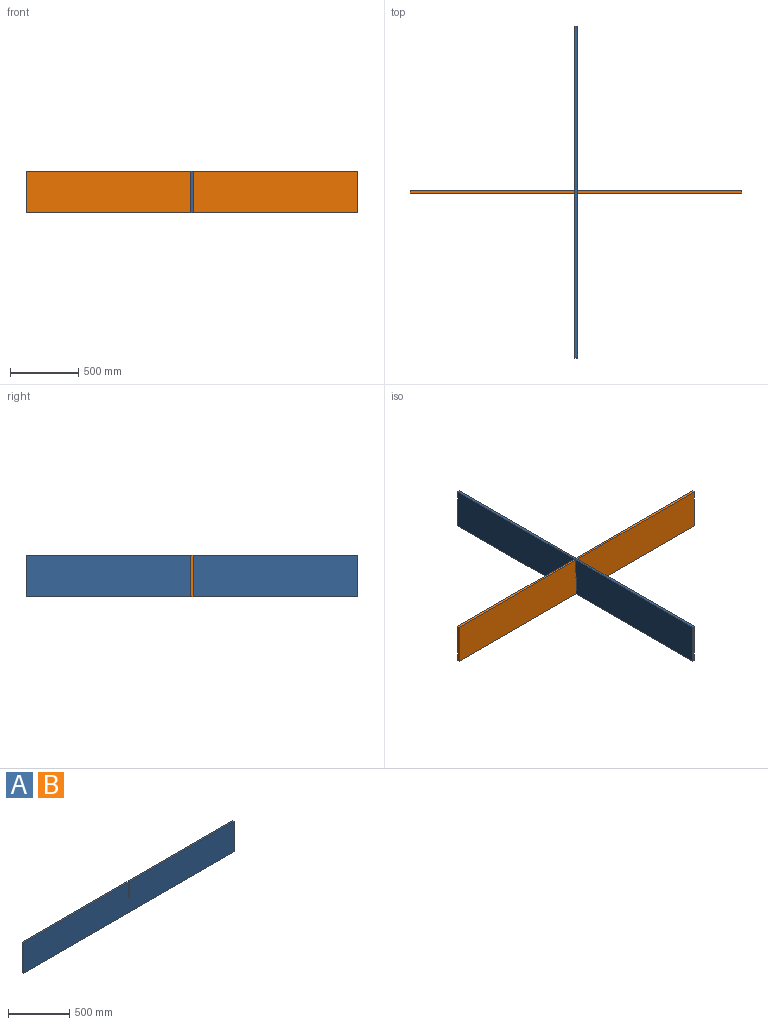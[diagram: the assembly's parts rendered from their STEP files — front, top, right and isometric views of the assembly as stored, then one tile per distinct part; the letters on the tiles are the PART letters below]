
ASSEMBLY  parts=2 mates=1
PART A: 10 faces, bbox 2438.4x19.1x304.8 mm
  f0: plane 1209.68x19.05mm, normal (0,0,1), area 23044.3mm2, adj f1,f7,f8,f9
  f1: plane 152.4x19.05mm, normal (-1,0,0), area 2903.2mm2, adj f0,f2,f8,f9
  f2: plane 19.05x19.05mm, normal (0,0,1), area 362.9mm2, adj f1,f3,f8,f9
  f3: plane 152.4x19.05mm, normal (1,0,0), area 2903.2mm2, adj f2,f4,f8,f9
  f4: plane 1209.68x19.05mm, normal (0,0,1), area 23044.3mm2, adj f3,f5,f8,f9
  f5: plane 304.8x19.05mm, normal (-1,0,0), area 5806.4mm2, adj f4,f6,f8,f9
  f6: plane 2438.4x19.05mm, normal (0,0,-1), area 46451.5mm2, adj f5,f7,f8,f9
  f7: plane 304.8x19.05mm, normal (1,0,0), area 5806.4mm2, adj f0,f6,f8,f9
  f8: plane 2438.4x304.8mm, normal (0,-1,0), area 740321.1mm2, adj f0,f1,f2,f3,f4,f5,f6,f7
  f9: plane 2438.4x304.8mm, normal (0,1,0), area 740321.1mm2, adj f0,f1,f2,f3,f4,f5,f6,f7
PART B: same geometry as A
PLACE A rot(axis=(0.71,0.71,0),180deg) t=(246.52,-390.51,217.68)mm
PLACE B t=(-433.05,289.06,210.44)mm
MATE fastened A.f2 <-> B.f2  axis (0,0,-1) through (236.99,279.53,214.06)mm
